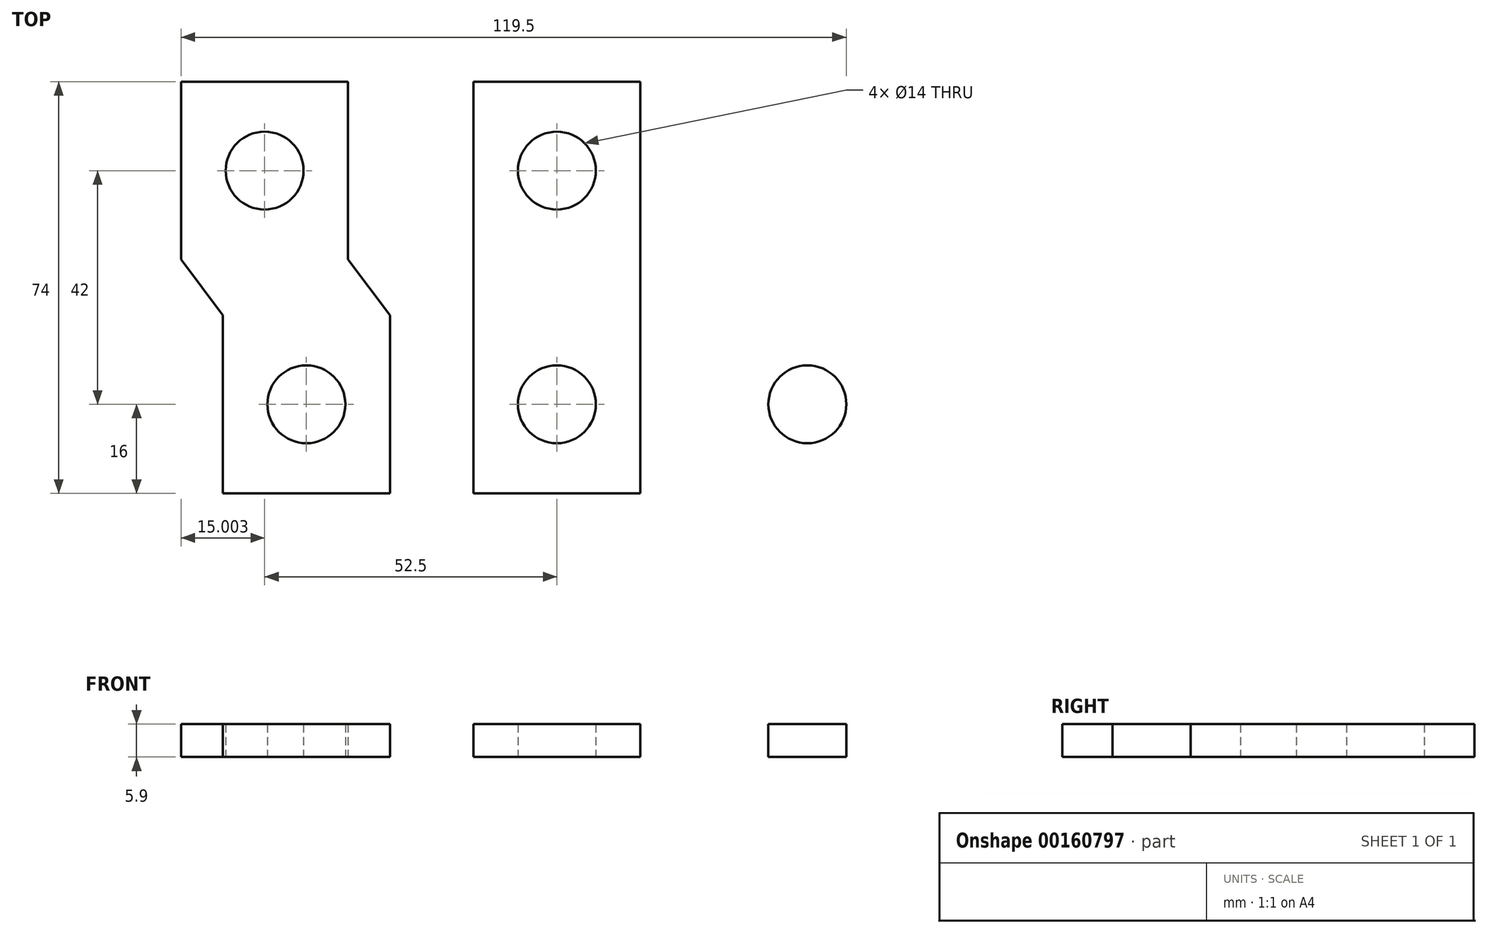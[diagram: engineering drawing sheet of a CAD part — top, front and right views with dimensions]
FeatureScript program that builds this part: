
annotation { "Feature Type Name" : "Feature", "Feature Type Description" : "" }
export const myFeature = defineFeature(function(context is Context, id is Id, definition is map)
    precondition{}
    {
        {
            var Q0;
            Q0=qCreatedBy(makeId("Top.planeOp"),FACE);
            var sketch = newSketch(context, id + "F0", { "sketchPlane" : qUnion([Q0])});
            skCircle(sketch, "E0.1.0.0", {"center": v(4.6, -21) * mm, "radius": 7 * mm});
            skLineSegment(sketch, "E1.MirrorCS", {"start": v(72.1, 37) * mm, "end": v(42.1, 37) * mm});
            skCircle(sketch, "E2.MirrorC", {"center": v(49.6, -21) * mm, "radius": 7 * mm});
            skLineSegment(sketch, "E3.top", {"start": v(-10.4, 37) * mm, "end": v(19.6, 37) * mm});
            skLineSegment(sketch, "E3.left", {"start": v(-10.4, -37) * mm, "end": v(-10.4, 37) * mm});
            skLineSegment(sketch, "E3.right", {"start": v(19.6, -37) * mm, "end": v(19.6, 37) * mm});
            skPoint(sketch, "E4", {"position": v(4.6, 21) * mm});
            skPoint(sketch, "E4.positionSnap0", {"position": v(4.6, 37) * mm});
            skCircle(sketch, "E5", {"center": v(4.6, 21) * mm, "radius": 7 * mm});
            skPoint(sketch, "E6", {"position": v(57.1, 37) * mm});
            skLineSegment(sketch, "E7", {"start": v(19.6, -37) * mm, "end": v(-10.4, -37) * mm});
            skPoint(sketch, "E8", {"position": v(57.1, 21) * mm});
            skCircle(sketch, "E9", {"center": v(57.1, 21) * mm, "radius": 7 * mm});
            skLineSegment(sketch, "E10.top", {"start": v(64.6, -37) * mm, "end": v(34.6, -37) * mm});
            skLineSegment(sketch, "E10.left", {"start": v(64.6, -5) * mm, "end": v(64.6, -37) * mm});
            skLineSegment(sketch, "E10.right", {"start": v(34.6, -5) * mm, "end": v(34.6, -37) * mm});
            skLineSegment(sketch, "E11.left", {"start": v(72.1, 37) * mm, "end": v(72.1, 5) * mm});
            skLineSegment(sketch, "E12", {"start": v(42.1, 5) * mm, "end": v(42.1, 37) * mm});
            skLineSegment(sketch, "E13", {"start": v(34.6, -5) * mm, "end": v(42.1, 5) * mm});
            skLineSegment(sketch, "E14", {"start": v(64.6, -5) * mm, "end": v(72.1, 5) * mm});
            skLineSegment(sketch, "E15", {"start": v(4.6, 37) * mm, "end": v(4.6, 84.85) * mm});
            skLineSegment(sketch, "E16.MirrorCS", {"start": v(-62.9, 37) * mm, "end": v(-32.9, 37) * mm});
            skLineSegment(sketch, "E17.MirrorCS", {"start": v(-55.4, -5) * mm, "end": v(-55.4, -37) * mm});
            skPoint(sketch, "E18.MirrorP", {"position": v(-47.9, 37) * mm});
            skPoint(sketch, "E19.MirrorP", {"position": v(-40.4, -21) * mm});
            skCircle(sketch, "E20.MirrorC", {"center": v(-40.4, -21) * mm, "radius": 7 * mm});
            skLineSegment(sketch, "E21.MirrorCS", {"start": v(-62.9, 37) * mm, "end": v(-62.9, 5) * mm});
            skLineSegment(sketch, "E22.MirrorCS", {"start": v(-25.4, -5) * mm, "end": v(-25.4, -37) * mm});
            skCircle(sketch, "E23.MirrorC", {"center": v(-47.9, 21) * mm, "radius": 7 * mm});
            skLineSegment(sketch, "E24.MirrorCS", {"start": v(-32.9, 5) * mm, "end": v(-32.9, 37) * mm});
            skLineSegment(sketch, "E25.MirrorCS", {"start": v(-55.4, -5) * mm, "end": v(-62.9, 5) * mm});
            skLineSegment(sketch, "E26.MirrorCS", {"start": v(-55.4, -37) * mm, "end": v(-25.4, -37) * mm});
            skLineSegment(sketch, "E27.MirrorCS", {"start": v(-25.4, -5) * mm, "end": v(-32.9, 5) * mm});
            skSolve(sketch);
        }
        {
            var Q0;
            Q0=makeQuery(id+"F0.imprint","IMPRINT",FACE,{"disambiguationData":[TD([[makeQuery(id+"F0.imprint","IMPRINT",EDGE,{"derivedFrom":sQuery(id+"F0.wireOp",EDGE,"E17.MirrorCS")}),1.0]])]});
            var Q1;
            Q1=makeQuery(id+"F0.imprint","IMPRINT",FACE,{"disambiguationData":[TD([[makeQuery(id+"F0.imprint","IMPRINT",EDGE,{"derivedFrom":sQuery(id+"F0.wireOp",EDGE,"E0.1.0.0")}),-1.0]])]});
            var Q2;
            Q2=makeQuery(id+"F0.imprint","IMPRINT",FACE,{"disambiguationData":[TD([[makeQuery(id+"F0.imprint","IMPRINT",EDGE,{"derivedFrom":sQuery(id+"F0.wireOp",EDGE,"E2.MirrorC")}),1.0]])]});
            extrude(context, id + "F1", {"entities" : qUnion([Q0, Q1, Q2]), "depth" : 5.9 * mm});
        }
    });
